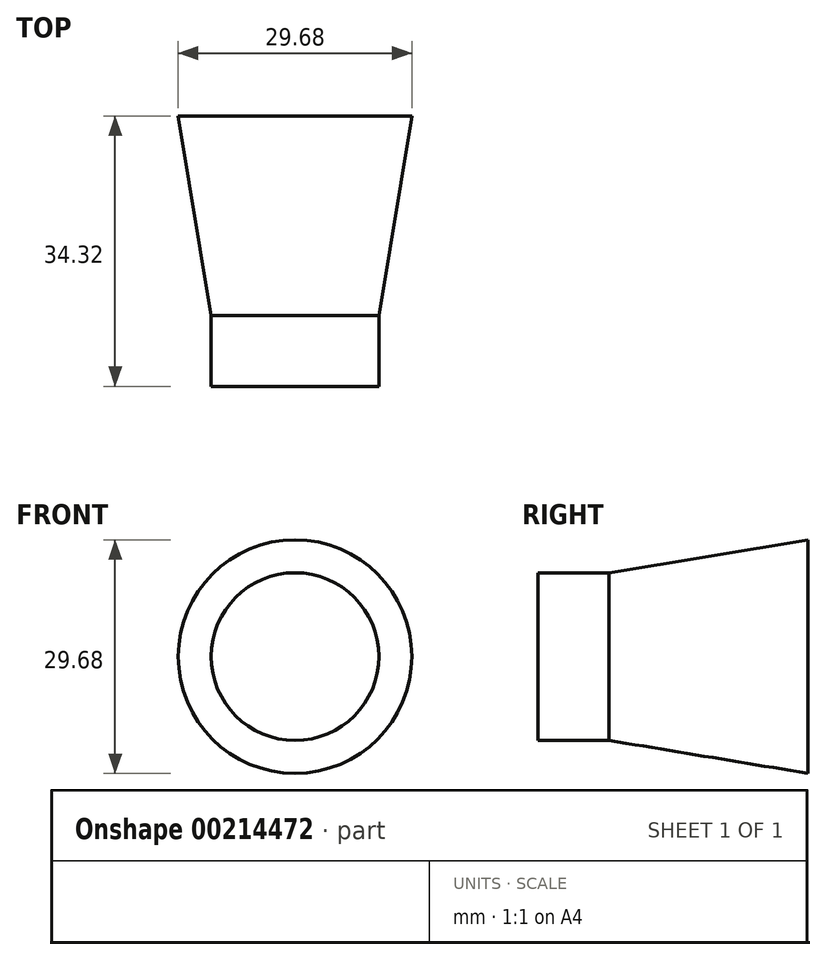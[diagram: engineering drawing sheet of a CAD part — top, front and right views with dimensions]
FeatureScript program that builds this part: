
annotation { "Feature Type Name" : "Feature", "Feature Type Description" : "" }
export const myFeature = defineFeature(function(context is Context, id is Id, definition is map)
    precondition{}
    {
        {
            var Q0;
            Q0=qCreatedBy(makeId("Top.planeOp"),FACE);
            var sketch = newSketch(context, id + "F0", { "sketchPlane" : qUnion([Q0])});
            skLineSegment(sketch, "E0", {"start": v(0, 0) * mm, "end": v(0, 34.32) * mm});
            skLineSegment(sketch, "E1", {"start": v(0, 34.32) * mm, "end": v(14.84, 34.32) * mm});
            skLineSegment(sketch, "E2", {"start": v(14.84, 34.32) * mm, "end": v(10.65, 9.01) * mm});
            skLineSegment(sketch, "E3", {"start": v(10.65, 9.01) * mm, "end": v(10.65, 0) * mm});
            skLineSegment(sketch, "E4", {"start": v(10.65, 0) * mm, "end": v(0, 0) * mm});
            skSolve(sketch);
        }
        {
            var Q0;
            Q0=makeQuery(id+"F0.imprint","IMPRINT",FACE,{"disambiguationData":[TD([[makeQuery(id+"F0.imprint","IMPRINT",EDGE,{"derivedFrom":sQuery(id+"F0.wireOp",EDGE,"E0")}),-1.0]])]});
            var Q1;
            Q1=sQuery(id+"F0.wireOp",EDGE,"E0");
            revolve(context, id + "F1", {"entities" : qUnion([Q0]), "axis" : qUnion([Q1]), "revolveType" : RevolveType.FULL});
        }
    });
